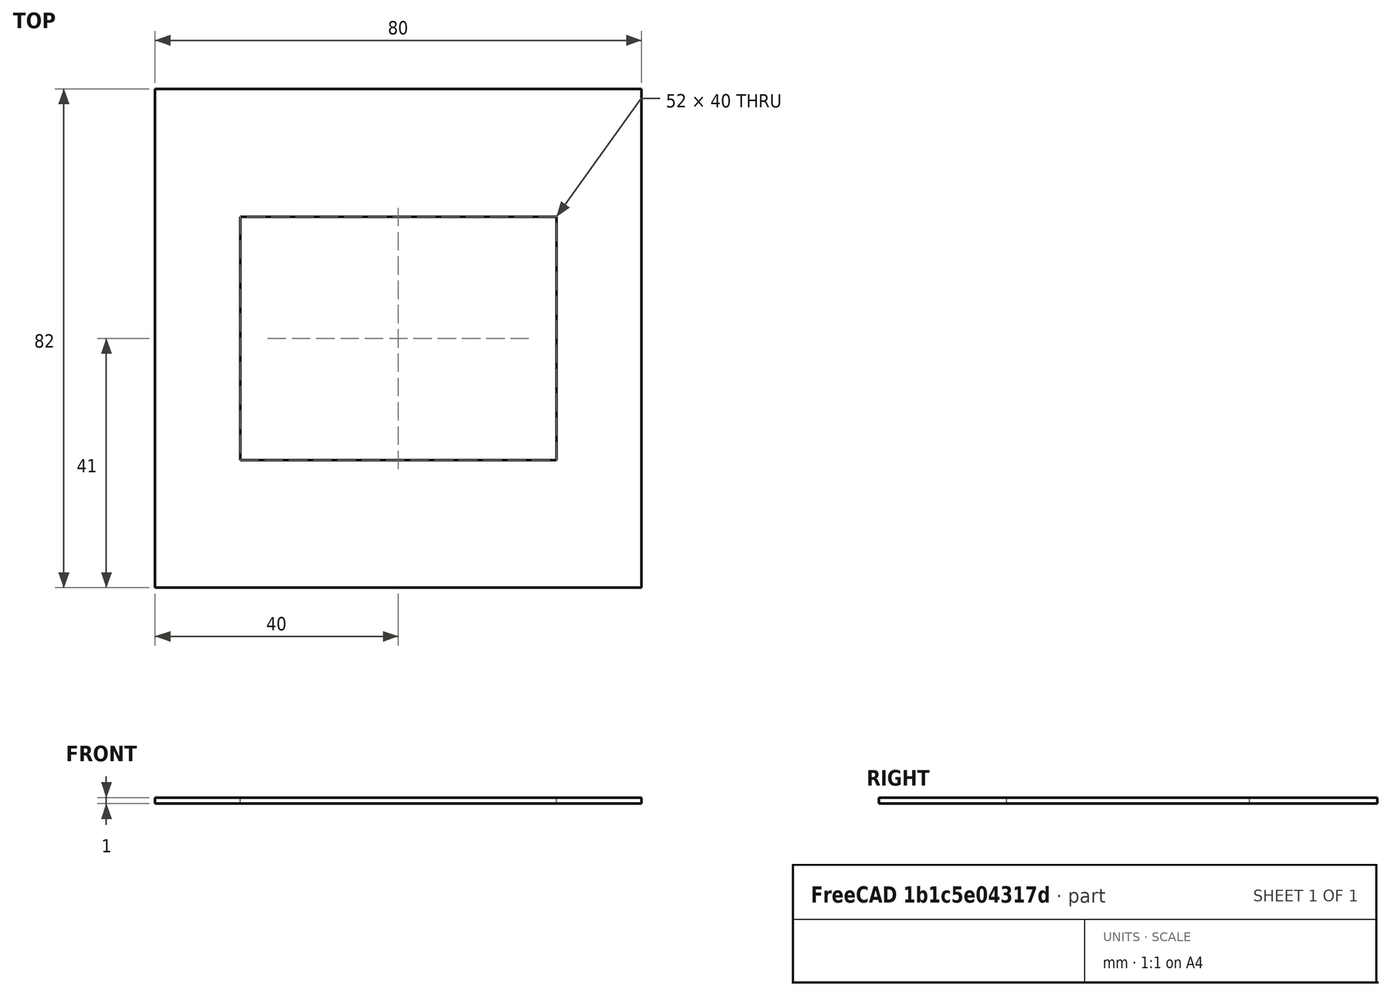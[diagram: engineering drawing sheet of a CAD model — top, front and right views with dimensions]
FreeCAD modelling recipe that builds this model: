
FCSTD DOCUMENT  (FreeCAD 0.16R6712 (Git))
Label: Cut_Marking_G366
License: All rights reserved
LicenseURL: http://en.wikipedia.org/wiki/All_rights_reserved
objects: Drawing::FeatureViewPython×4, Sketcher::SketchObject×1, PartDesign::Pad×1, Drawing::FeatureViewPart×1, Drawing::FeaturePage×1
note: 3 computed .brp shape members not serialized (recipe doc carries the construction recipe); baked Part::Feature solids carry a one-line shape summary decoded from their .brp

FEATURE [Sketcher::SketchObject] Sketch
  sketch-geometry (8):
    g0: LineSegment StartX=0 StartY=0 StartZ=0 EndX=80 EndY=0 EndZ=0
    g1: LineSegment StartX=80 StartY=0 StartZ=0 EndX=80 EndY=82 EndZ=0
    g2: LineSegment StartX=80 StartY=82 StartZ=0 EndX=0 EndY=82 EndZ=0
    g3: LineSegment StartX=0 StartY=82 StartZ=0 EndX=0 EndY=0 EndZ=0
    g4: LineSegment StartX=14 StartY=61 StartZ=0 EndX=66 EndY=61 EndZ=0
    g5: LineSegment StartX=66 StartY=61 StartZ=0 EndX=66 EndY=21 EndZ=0
    g6: LineSegment StartX=66 StartY=21 StartZ=0 EndX=14 EndY=21 EndZ=0
    g7: LineSegment StartX=14 StartY=21 StartZ=0 EndX=14 EndY=61 EndZ=0
  constraints (23):
    c: Coincident(g0,g1)
    c: Coincident(g1,g2)
    c: Coincident(g2,g3)
    c: Coincident(g3,g0)
    c: Horizontal(g0)
    c: Horizontal(g2)
    c: Vertical(g1)
    c: Vertical(g3)
    c: Coincident(g0,g-1)
    c: Distance(g2) = 80
    c: Distance(g3) = 82
    c: Coincident(g4,g5)
    c: Coincident(g5,g6)
    c: Coincident(g6,g7)
    c: Coincident(g7,g4)
    c: Horizontal(g4)
    c: Horizontal(g6)
    c: Vertical(g5)
    c: Vertical(g7)
    c: Distance(g4) = 52
    c: Distance(g7) = 40
    c: DistanceY(g-1,g6) = 21
    c: DistanceX(g-1,g6) = 14
FEATURE [PartDesign::Pad] Pad
  Length = 1
  Length2 = 100
  Sketch = -> Sketch
  Type = 0
FEATURE [Drawing::FeatureViewPart] Ortho005  label="Ortho_0_-1"
  Direction = (0,0,-1)
  HiddenWidth = 0.15
  LineWidth = 0.35
  Rotation = 0
  ShowHiddenLines = false
  ShowSmoothLines = false
  Source = -> Pad
  Tolerance = 0.05
  ViewResult = <g id="Ortho_0_-1"\n   transform="rotate(0,180,120) translate(180,120) scale(1,1)"\n  >\n<g   stroke="rgb(0, 0, 0)"\n   stroke-width="0.35"\n   stroke-linecap="butt"\n   stroke-linejoin="miter"\n   fill="none"\n   transform="scale(1,-1)"\n  >\n<path id= "1" d=" M 0 0 L -80 0 " />\n<path id= "2" d=" M -80 0 L -80 82 " />\n<path id= "3" d=" M -80 82 L 0 82 " />\n<path id= "4" d=" M 0 82 L 0 0 " />\n<path id= "5" d=" M -14 61 L -66 61 " />\n<path id= "6" d=" M -66 61 L -66 21 " />\n<path id= "7" d=" M -66 21 L -14 21 " />\n<path id= "8" d=" M -14 21 L -14 61 " />\n</g>\n</g>
  Visible = true
  X = 180
  Y = 120
FEATURE [Drawing::FeatureViewPython] dim001  # drawing view (typed FeaturePython)
  Rotation = 0
  ViewResult = <g> \n  <line x1="100.000000" y1="122.000000" x2="100.000000" y2="141.000000" style="stroke:rgb(0,0,255);stroke-width:0.50" />\n<line x1="180.000000" y1="122.000000" x2="180.000000" y2="141.000000" style="stroke:rgb(0,0,255);stroke-width:0.50" />\n<line x1="100.000000" y1="140.000000" x2="180.000000" y2="140.000000" style="stroke:rgb(0,0,255);stroke-width:0.50" /> \n  <polygon points="180.000000,140.000000 177.000000,139.000000 176.000000,140.000000 177.000000,141.000000" style="fill:rgb(0,0,255);stroke:rgb(0,0,255);stroke-width:0" /><polygon points="100.000000,140.000000 103.000000,141.000000 104.000000,140.000000 103.000000,139.000000" style="fill:rgb(0,0,255);stroke:rgb(0,0,255);stroke-width:0" /> \n  <text x="140.000000" y="138.000000" font-family="inherit" font-size="3.6" fill="rgb(0,0,255)" text-anchor="middle" transform="rotate(0.000000 140.000000,138.000000)" >80</text> </g>
  Visible = true
  X = 0
  Y = 0
  arrowL1 = 3
  arrowL2 = 1
  arrowW = 2
  arrow_scheme = 0
  autoPlaceOffset = 2
  autoPlaceText = true
  click1_x = 170
  click1_y = 140
  click2_x = 170
  click2_y = 140
  comma_decimal_place = false
  dimension_line_overshoot = 1
  gap_datum_points = 2
  halfDimension_linear = false
  lineColor = rgb(0,0,255)
  strokeWidth = 0.5
  textFormat_linear = %(value)3.3f
  textRenderer_color = rgb(0,0,255)
  textRenderer_family = inherit
  textRenderer_size = 3.6
  unit_custom_scale = 1
  unit_scheme = 0
FEATURE [Drawing::FeatureViewPython] dim002  # drawing view (typed FeaturePython)
  Rotation = 0
  ViewResult = <g> \n  <line x1="182.000000" y1="38.000000" x2="206.000000" y2="38.000000" style="stroke:rgb(0,0,255);stroke-width:0.50" />\n<line x1="182.000000" y1="120.000000" x2="206.000000" y2="120.000000" style="stroke:rgb(0,0,255);stroke-width:0.50" />\n<line x1="205.000000" y1="38.000000" x2="205.000000" y2="120.000000" style="stroke:rgb(0,0,255);stroke-width:0.50" /> \n  <polygon points="205.000000,120.000000 206.000000,117.000000 205.000000,116.000000 204.000000,117.000000" style="fill:rgb(0,0,255);stroke:rgb(0,0,255);stroke-width:0" /><polygon points="205.000000,38.000000 204.000000,41.000000 205.000000,42.000000 206.000000,41.000000" style="fill:rgb(0,0,255);stroke:rgb(0,0,255);stroke-width:0" /> \n  <text x="203.000000" y="79.000000" font-family="inherit" font-size="3.6" fill="rgb(0,0,255)" text-anchor="middle" transform="rotate(-90.000000 203.000000,79.000000)" >82</text> </g>
  Visible = true
  X = 0
  Y = 0
  arrowL1 = 3
  arrowL2 = 1
  arrowW = 2
  arrow_scheme = 0
  autoPlaceOffset = 2
  autoPlaceText = true
  click1_x = 205
  click1_y = 115
  click2_x = 205
  click2_y = 115
  comma_decimal_place = false
  dimension_line_overshoot = 1
  gap_datum_points = 2
  halfDimension_linear = false
  lineColor = rgb(0,0,255)
  strokeWidth = 0.5
  textFormat_linear = %(value)3.3f
  textRenderer_color = rgb(0,0,255)
  textRenderer_family = inherit
  textRenderer_size = 3.6
  unit_custom_scale = 1
  unit_scheme = 0
FEATURE [Drawing::FeatureViewPython] dim003  # drawing view (typed FeaturePython)
  Rotation = 0
  ViewResult = <g> \n  <line x1="114.000000" y1="101.000000" x2="114.000000" y2="111.000000" style="stroke:rgb(0,0,255);stroke-width:0.50" />\n<line x1="166.000000" y1="101.000000" x2="166.000000" y2="111.000000" style="stroke:rgb(0,0,255);stroke-width:0.50" />\n<line x1="114.000000" y1="110.000000" x2="166.000000" y2="110.000000" style="stroke:rgb(0,0,255);stroke-width:0.50" /> \n  <polygon points="166.000000,110.000000 163.000000,109.000000 162.000000,110.000000 163.000000,111.000000" style="fill:rgb(0,0,255);stroke:rgb(0,0,255);stroke-width:0" /><polygon points="114.000000,110.000000 117.000000,111.000000 118.000000,110.000000 117.000000,109.000000" style="fill:rgb(0,0,255);stroke:rgb(0,0,255);stroke-width:0" /> \n  <text x="140.000000" y="108.000000" font-family="inherit" font-size="3.6" fill="rgb(0,0,255)" text-anchor="middle" transform="rotate(0.000000 140.000000,108.000000)" >52</text> </g>
  Visible = true
  X = 0
  Y = 0
  arrowL1 = 3
  arrowL2 = 1
  arrowW = 2
  arrow_scheme = 0
  autoPlaceOffset = 2
  autoPlaceText = true
  click1_x = 165
  click1_y = 110
  click2_x = 165
  click2_y = 110
  comma_decimal_place = false
  dimension_line_overshoot = 1
  gap_datum_points = 2
  halfDimension_linear = false
  lineColor = rgb(0,0,255)
  strokeWidth = 0.5
  textFormat_linear = %(value)3.3f
  textRenderer_color = rgb(0,0,255)
  textRenderer_family = inherit
  textRenderer_size = 3.6
  unit_custom_scale = 1
  unit_scheme = 0
FEATURE [Drawing::FeatureViewPython] dim004  # drawing view (typed FeaturePython)
  Rotation = 0
  ViewResult = <g> \n  <line x1="168.000000" y1="59.000000" x2="176.000000" y2="59.000000" style="stroke:rgb(0,0,255);stroke-width:0.50" />\n<line x1="168.000000" y1="99.000000" x2="176.000000" y2="99.000000" style="stroke:rgb(0,0,255);stroke-width:0.50" />\n<line x1="175.000000" y1="59.000000" x2="175.000000" y2="99.000000" style="stroke:rgb(0,0,255);stroke-width:0.50" /> \n  <polygon points="175.000000,99.000000 176.000000,96.000000 175.000000,95.000000 174.000000,96.000000" style="fill:rgb(0,0,255);stroke:rgb(0,0,255);stroke-width:0" /><polygon points="175.000000,59.000000 174.000000,62.000000 175.000000,63.000000 176.000000,62.000000" style="fill:rgb(0,0,255);stroke:rgb(0,0,255);stroke-width:0" /> \n  <text x="173.000000" y="79.000000" font-family="inherit" font-size="3.6" fill="rgb(0,0,255)" text-anchor="middle" transform="rotate(-90.000000 173.000000,79.000000)" >40</text> </g>
  Visible = true
  X = 0
  Y = 0
  arrowL1 = 3
  arrowL2 = 1
  arrowW = 2
  arrow_scheme = 0
  autoPlaceOffset = 2
  autoPlaceText = true
  click1_x = 175
  click1_y = 100
  click2_x = 175
  click2_y = 100
  comma_decimal_place = false
  dimension_line_overshoot = 1
  gap_datum_points = 2
  halfDimension_linear = false
  lineColor = rgb(0,0,255)
  strokeWidth = 0.5
  textFormat_linear = %(value)3.3f
  textRenderer_color = rgb(0,0,255)
  textRenderer_family = inherit
  textRenderer_size = 3.6
  unit_custom_scale = 1
  unit_scheme = 0
FEATURE [Drawing::FeaturePage] Page
  EditableTexts = Designed by Name | Date | Scale | Weight | Title | Subtitle | Drawing number | Sheet
  Group = -> [Ortho005,dim001,dim002,dim003,dim004]
